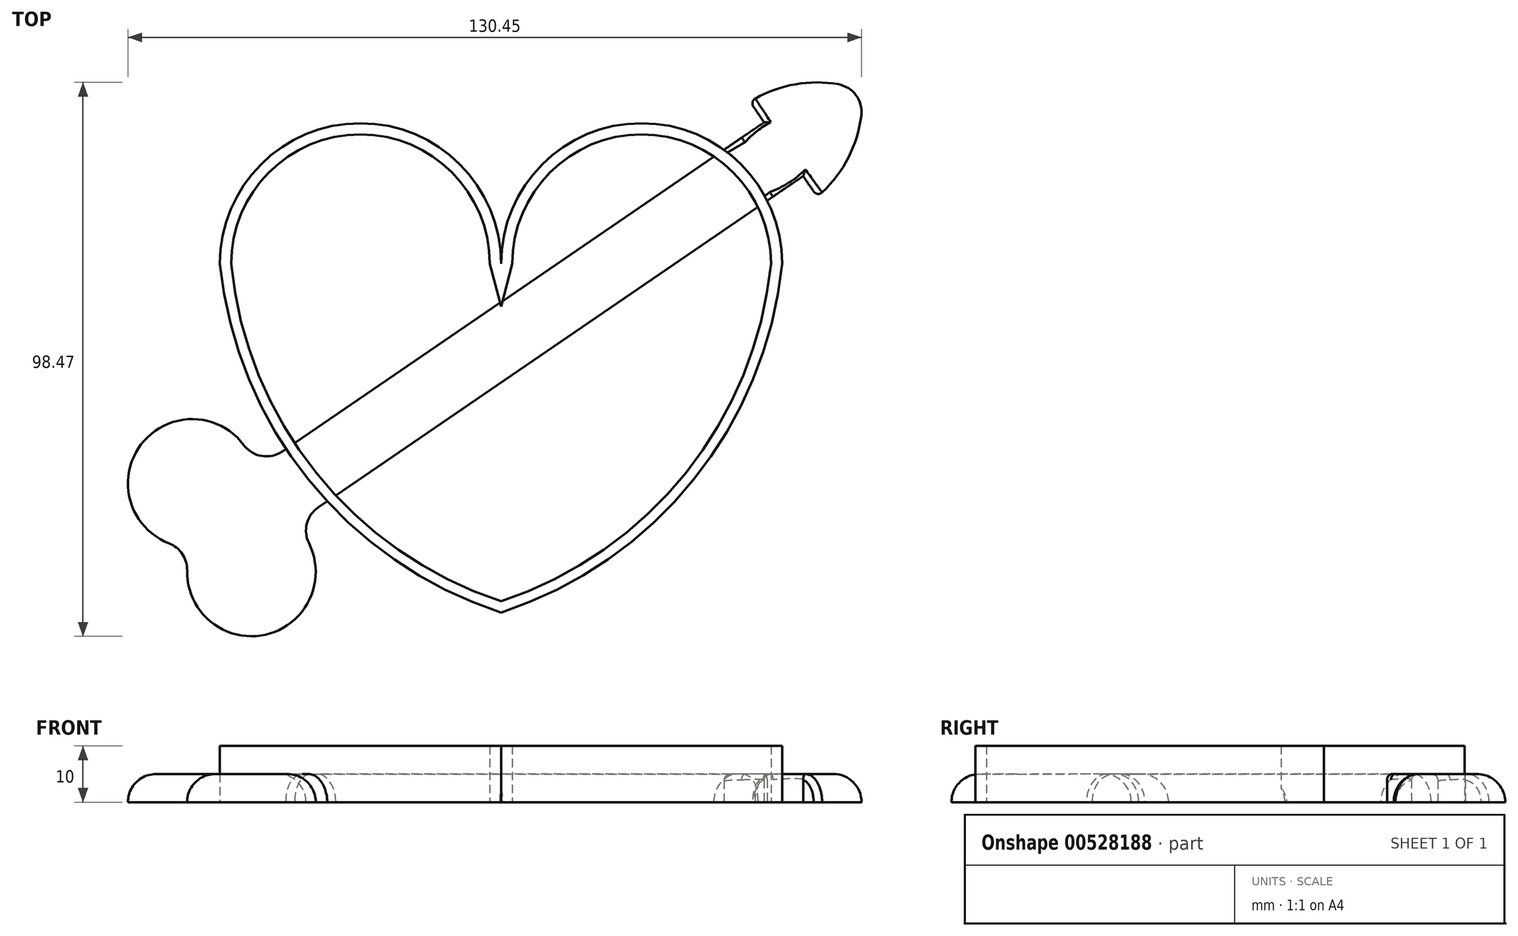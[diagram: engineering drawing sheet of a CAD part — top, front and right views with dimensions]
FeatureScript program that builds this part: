
annotation { "Feature Type Name" : "Feature", "Feature Type Description" : "" }
export const myFeature = defineFeature(function(context is Context, id is Id, definition is map)
    precondition{}
    {
        {
            var Q0;
            Q0=qCreatedBy(makeId("Top.planeOp"),FACE);
            var sketch = newSketch(context, id + "F0", { "sketchPlane" : qUnion([Q0])});
            skArc(sketch, "E0", {"start": v(0, 0) * mm, "mid": v(-25, 25) * mm, "end": v(-50, 0) * mm});
            skArc(sketch, "E1", {"start": v(-50, 0) * mm, "mid": v(-34.2, -38.43) * mm, "end": v(0, -62) * mm});
            skArc(sketch, "E2", {"start": v(-2, 0) * mm, "mid": v(-25, 23) * mm, "end": v(-48, 0) * mm});
            skArc(sketch, "E3", {"start": v(-48, 0) * mm, "mid": v(-32.9, -37.12) * mm, "end": v(0, -60) * mm});
            skArc(sketch, "E4.MirrorCS", {"start": v(0, 0) * mm, "mid": v(25, 25) * mm, "end": v(50, 0) * mm});
            skArc(sketch, "E5.MirrorCS", {"start": v(2, 0) * mm, "mid": v(25, 23) * mm, "end": v(48, 0) * mm});
            skArc(sketch, "E6.MirrorCS", {"start": v(48, 0) * mm, "mid": v(32.9, -37.12) * mm, "end": v(0, -60) * mm});
            skArc(sketch, "E7.MirrorCS", {"start": v(50, 0) * mm, "mid": v(34.2, -38.43) * mm, "end": v(0, -62) * mm});
            skLineSegment(sketch, "E8", {"start": v(-2, 0) * mm, "end": v(0, -7.62) * mm});
            skLineSegment(sketch, "E9", {"start": v(0, -7.62) * mm, "end": v(2, 0) * mm});
            skSolve(sketch);
        }
        {
            var Q0;
            {var subQ1=sQuery(id+"F0.wireOp",EDGE,"E0");Q0=makeQuery(id+"F0.imprint","IMPRINT",FACE,{"disambiguationData":[TD([[makeQuery(id+"F0.imprint","IMPRINT",EDGE,{"derivedFrom":subQ1}),1.0]])]});}
            extrude(context, id + "F1", {"entities" : qUnion([Q0]), "depth" : 10 * mm, "offsetDistance" : 25 * mm});
        }
        {
            var Q0;
            Q0=qCreatedBy(makeId("Top.planeOp"),FACE);
            var sketch = newSketch(context, id + "F2", { "sketchPlane" : qUnion([Q0])});
            skLineSegment(sketch, "E10", {"start": v(-38.9, -33.37) * mm, "end": v(46.78, 25.15) * mm});
            skLineSegment(sketch, "E11", {"start": v(53.71, 15.59) * mm, "end": v(-32.5, -43.3) * mm});
            skArc(sketch, "E12", {"start": v(-45.73, -32.23) * mm, "mid": v(-64.02, -32.13) * mm, "end": v(-59.02, -49.72) * mm});
            skArc(sketch, "E13", {"start": v(-55.82, -54.5) * mm, "mid": v(-41.9, -65.94) * mm, "end": v(-34.16, -49.67) * mm});
            skLineSegment(sketch, "E14", {"start": v(46.78, 25.15) * mm, "end": v(44.27, 28.82) * mm});
            skLineSegment(sketch, "E15", {"start": v(53.71, 15.59) * mm, "end": v(56.22, 11.92) * mm});
            skArc(sketch, "E16", {"start": v(59.95, 31.92) * mm, "mid": v(51.82, 31.82) * mm, "end": v(44.27, 28.82) * mm});
            skArc(sketch, "E17", {"start": v(56.22, 11.92) * mm, "mid": v(61.52, 18.41) * mm, "end": v(64.06, 26.4) * mm});
            skPoint(sketch, "E18.visualSharp", {"position": v(64.16, 30.77) * mm});
            skArc(sketch, "E18.filletArc", {"start": v(64.06, 26.4) * mm, "mid": v(63.1, 29.99) * mm, "end": v(59.95, 31.92) * mm});
            skPoint(sketch, "E19.visualSharp", {"position": v(-43.72, -36.67) * mm});
            skArc(sketch, "E19.filletArc", {"start": v(-45.73, -32.23) * mm, "mid": v(-42.54, -34.18) * mm, "end": v(-38.9, -33.37) * mm});
            skPoint(sketch, "E20.visualSharp", {"position": v(-36.79, -46.23) * mm});
            skArc(sketch, "E20.filletArc", {"start": v(-32.5, -43.3) * mm, "mid": v(-34.52, -46.18) * mm, "end": v(-34.16, -49.67) * mm});
            skPoint(sketch, "E21.visualSharp", {"position": v(-54.98, -50.48) * mm});
            skArc(sketch, "E21.filletArc", {"start": v(-55.82, -54.5) * mm, "mid": v(-56.66, -51.6) * mm, "end": v(-59.02, -49.72) * mm});
            skSolve(sketch);
        }
        {
            var Q0;
            Q0=makeQuery(id+"F2.imprint","IMPRINT",FACE,{"disambiguationData":[TD([[makeQuery(id+"F2.imprint","IMPRINT",EDGE,{"derivedFrom":sQuery(id+"F2.wireOp",EDGE,"E10")}),-1.0]])]});
            extrude(context, id + "F3", {"entities" : qUnion([Q0]), "operationType" : NewBodyOperationType.ADD, "depth" : 5 * mm, "offsetDistance" : 25 * mm});
        }
        {
            var Q0;
            Q0=makeQuery(id+"F3.opExtrude","CAP_EDGE",EDGE,{"disambiguationData":[OSD([sQuery(id+"F2.wireOp",EDGE,"E13")])],"isStart":false});
            var Q1;
            {var subQ0=sQuery(id+"F2.wireOp",EDGE,"E11");Q1=makeQuery(id+"F3.boolean.opBoolean","SPLIT",EDGE,{"disambiguationData":[TD([makeQuery(id+"F1.opExtrude","SWEPT_FACE",FACE,{"disambiguationData":[OSD([sQuery(id+"F0.wireOp",EDGE,"E3")])]})])],"derivedFrom":makeQuery(id+"F3.opExtrude","CAP_EDGE",EDGE,{"disambiguationData":[OSD([subQ0])],"isStart":false})});}
            var Q2;
            {var subQ0=sQuery(id+"F2.wireOp",EDGE,"E10");Q2=makeQuery(id+"F3.boolean.opBoolean","SPLIT",EDGE,{"disambiguationData":[TD([makeQuery(id+"F1.opExtrude","SWEPT_FACE",FACE,{"disambiguationData":[OSD([sQuery(id+"F0.wireOp",EDGE,"E3")])]})])],"derivedFrom":makeQuery(id+"F3.opExtrude","CAP_EDGE",EDGE,{"disambiguationData":[OSD([subQ0])],"isStart":false})});}
            var Q3;
            Q3=makeQuery(id+"F3.opExtrude","CAP_EDGE",EDGE,{"disambiguationData":[OSD([sQuery(id+"F2.wireOp",EDGE,"E16")])],"isStart":false});
            fillet(context, id + "F4", {"entities" : qUnion([Q0, Q1, Q2, Q3]), "radius" : 5 * mm, "tangentPropagation" : true, "allowEdgeOverflow" : false});
        }
        {
            var Q0;
            {var subQ5=sQuery(id+"F2.wireOp",EDGE,"E16");var subQ11=sQuery(id+"F2.wireOp",EDGE,"E10");var subQ12=sQuery(id+"F0.wireOp",EDGE,"E4.MirrorCS");Q0=makeQuery(id+"F4.opFillet","BLEND_EDGE",EDGE,{"blendedFrom":[makeQuery(id+"F3.opExtrude","CAP_EDGE",EDGE,{"disambiguationData":[OSD([subQ5])],"isStart":false}),makeQuery(id+"F3.boolean.opBoolean","SPLIT",FACE,{"disambiguationData":[TD([makeQuery(id+"F1.opExtrude","SWEPT_FACE",FACE,{"disambiguationData":[OSD([subQ12])]})])],"derivedFrom":makeQuery(id+"F3.opExtrude","SWEPT_FACE",FACE,{"disambiguationData":[OSD([subQ11])]})})],"blendedInto":[makeQuery(id+"F3.boolean.opBoolean","SPLIT",FACE,{"disambiguationData":[TD([makeQuery(id+"F1.opExtrude","SWEPT_FACE",FACE,{"disambiguationData":[OSD([subQ12])]})])],"derivedFrom":makeQuery(id+"F3.opExtrude","SWEPT_FACE",FACE,{"disambiguationData":[OSD([subQ11])]})})]});}
            var Q1;
            {var subQ4=sQuery(id+"F2.wireOp",EDGE,"E17");var subQ10=sQuery(id+"F2.wireOp",EDGE,"E11");var subQ12=sQuery(id+"F0.wireOp",EDGE,"E4.MirrorCS");Q1=makeQuery(id+"F4.opFillet","BLEND_EDGE",EDGE,{"blendedFrom":[makeQuery(id+"F3.opExtrude","CAP_EDGE",EDGE,{"disambiguationData":[OSD([subQ4])],"isStart":false}),makeQuery(id+"F3.boolean.opBoolean","SPLIT",FACE,{"disambiguationData":[TD([makeQuery(id+"F1.opExtrude","SWEPT_FACE",FACE,{"disambiguationData":[OSD([subQ12])]})])],"derivedFrom":makeQuery(id+"F3.opExtrude","SWEPT_FACE",FACE,{"disambiguationData":[OSD([subQ10])]})})],"blendedInto":[makeQuery(id+"F3.boolean.opBoolean","SPLIT",FACE,{"disambiguationData":[TD([makeQuery(id+"F1.opExtrude","SWEPT_FACE",FACE,{"disambiguationData":[OSD([subQ12])]})])],"derivedFrom":makeQuery(id+"F3.opExtrude","SWEPT_FACE",FACE,{"disambiguationData":[OSD([subQ10])]})})]});}
            var Q2;
            Q2=makeQuery(id+"F4.opFillet","BLEND_EDGE",EDGE,{"blendedFrom":[makeQuery(id+"F3.opExtrude","CAP_EDGE",EDGE,{"disambiguationData":[OSD([sQuery(id+"F2.wireOp",EDGE,"E16")])],"isStart":false}),makeQuery(id+"F3.opExtrude","SWEPT_FACE",FACE,{"disambiguationData":[OSD([sQuery(id+"F2.wireOp",EDGE,"E14")])]})],"blendedInto":[makeQuery(id+"F3.opExtrude","SWEPT_FACE",FACE,{"disambiguationData":[OSD([sQuery(id+"F2.wireOp",EDGE,"E14")])]})]});
            var Q3;
            Q3=makeQuery(id+"F4.opFillet","BLEND_EDGE",EDGE,{"blendedFrom":[makeQuery(id+"F3.opExtrude","CAP_EDGE",EDGE,{"disambiguationData":[OSD([sQuery(id+"F2.wireOp",EDGE,"E17")])],"isStart":false}),makeQuery(id+"F3.opExtrude","SWEPT_FACE",FACE,{"disambiguationData":[OSD([sQuery(id+"F2.wireOp",EDGE,"E15")])]})],"blendedInto":[makeQuery(id+"F3.opExtrude","SWEPT_FACE",FACE,{"disambiguationData":[OSD([sQuery(id+"F2.wireOp",EDGE,"E15")])]})]});
            fillet(context, id + "F5", {"entities" : qUnion([Q0, Q1, Q2, Q3]), "radius" : 1 * mm, "tangentPropagation" : true, "allowEdgeOverflow" : false});
        }
    });
